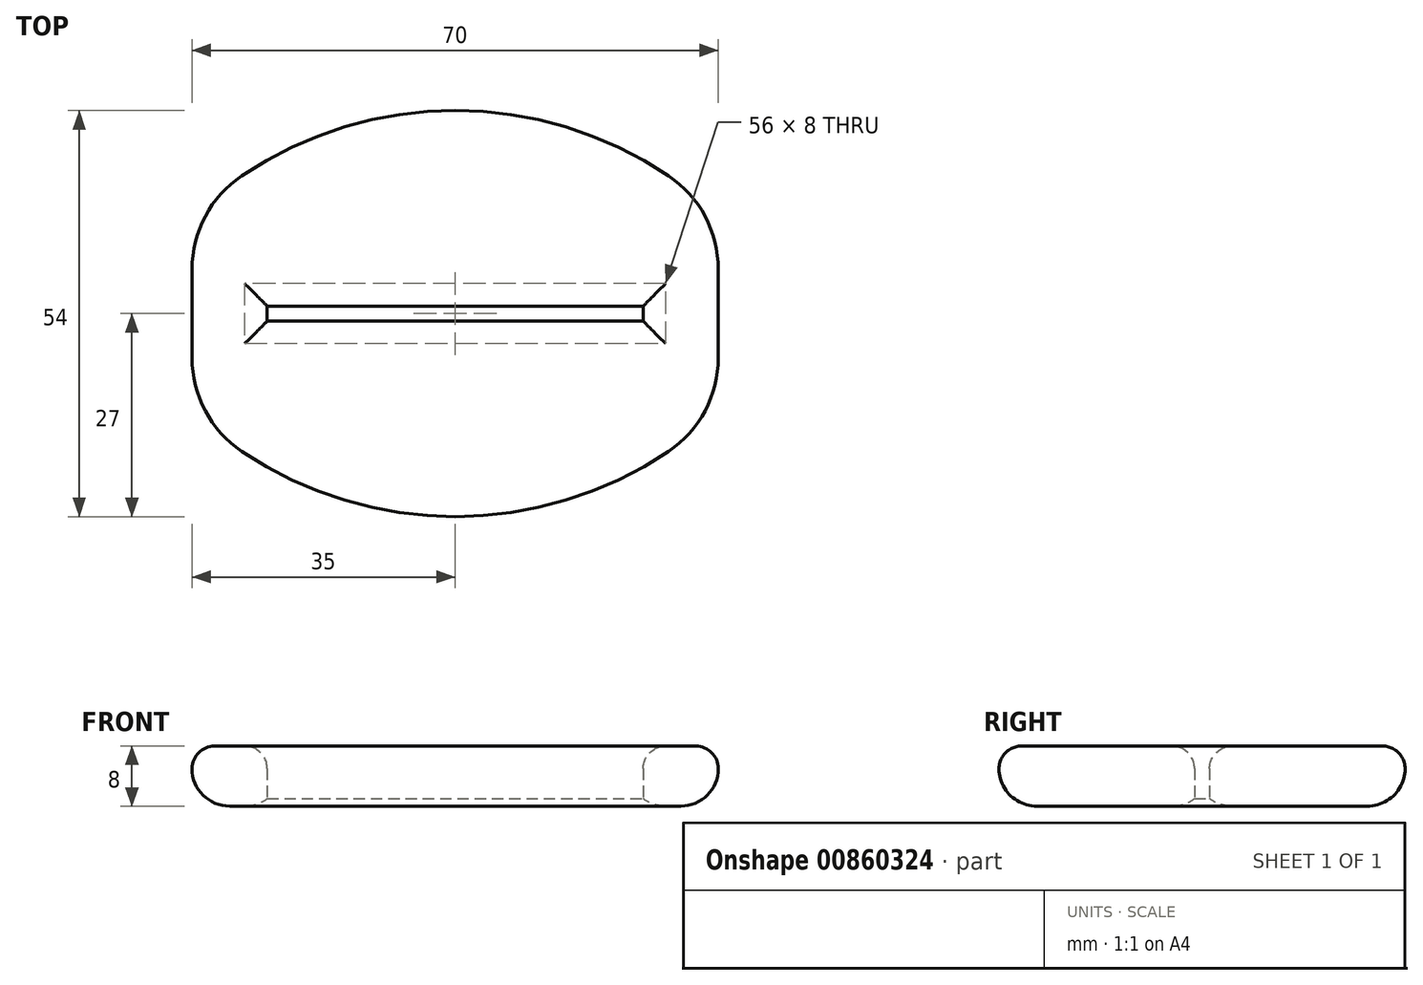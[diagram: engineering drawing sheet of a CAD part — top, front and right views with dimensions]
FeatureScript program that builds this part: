
annotation { "Feature Type Name" : "Feature", "Feature Type Description" : "" }
export const myFeature = defineFeature(function(context is Context, id is Id, definition is map)
    precondition{}
    {
        {
            var Q0;
            Q0=qCreatedBy(makeId("Top.planeOp"),FACE);
            var sketch = newSketch(context, id + "F0", { "sketchPlane" : qUnion([Q0])});
            skLineSegment(sketch, "E0.bottom", {"start": v(-25, 1) * mm, "end": v(25, 1) * mm});
            skLineSegment(sketch, "E0.top", {"start": v(-25, -1) * mm, "end": v(25, -1) * mm});
            skLineSegment(sketch, "E0.left", {"start": v(-25, 1) * mm, "end": v(-25, -1) * mm});
            skLineSegment(sketch, "E0.right", {"start": v(25, 1) * mm, "end": v(25, -1) * mm});
            skPoint(sketch, "E0.middle", {"position": v(0, 0) * mm});
            skLineSegment(sketch, "E1.bottom", {"start": v(-35, 13) * mm, "end": v(35, 13) * mm});
            skLineSegment(sketch, "E1.top", {"start": v(-35, -13) * mm, "end": v(35, -13) * mm});
            skLineSegment(sketch, "E1.left", {"start": v(-35, 13) * mm, "end": v(-35, -13) * mm});
            skLineSegment(sketch, "E1.right", {"start": v(35, 13) * mm, "end": v(35, -13) * mm});
            skArc(sketch, "E2", {"start": v(35, 13) * mm, "mid": v(0, 27) * mm, "end": v(-35, 13) * mm});
            skArc(sketch, "E3", {"start": v(-35, -13) * mm, "mid": v(0, -27) * mm, "end": v(35, -13) * mm});
            skSolve(sketch);
        }
        {
            var Q0;
            Q0=makeQuery(id+"F0.imprint","IMPRINT",FACE,{"disambiguationData":[TD([[makeQuery(id+"F0.imprint","IMPRINT",EDGE,{"derivedFrom":sQuery(id+"F0.wireOp",EDGE,"E1.bottom")}),1.0]])]});
            var Q1;
            Q1=makeQuery(id+"F0.imprint","IMPRINT",FACE,{"disambiguationData":[TD([[makeQuery(id+"F0.imprint","IMPRINT",EDGE,{"derivedFrom":sQuery(id+"F0.wireOp",EDGE,"E0.bottom")}),1.0]])]});
            var Q2;
            Q2=makeQuery(id+"F0.imprint","IMPRINT",FACE,{"disambiguationData":[TD([[makeQuery(id+"F0.imprint","IMPRINT",EDGE,{"derivedFrom":sQuery(id+"F0.wireOp",EDGE,"E1.top")}),-1.0]])]});
            extrude(context, id + "F1", {"entities" : qUnion([Q0, Q1, Q2]), "depth" : 8 * mm, "offsetDistance" : 25 * mm});
        }
        {
            var Q0;
            Q0=makeQuery(id+"F1.opExtrude","CAP_FACE",FACE,{"disambiguationData":[OSD([sQuery(id+"F0.wireOp",EDGE,"E0.bottom"),sQuery(id+"F0.wireOp",EDGE,"E0.top"),sQuery(id+"F0.wireOp",EDGE,"E0.left"),sQuery(id+"F0.wireOp",EDGE,"E0.right"),sQuery(id+"F0.wireOp",EDGE,"E1.bottom"),sQuery(id+"F0.wireOp",EDGE,"E1.top"),sQuery(id+"F0.wireOp",EDGE,"E1.left"),sQuery(id+"F0.wireOp",EDGE,"E1.right")])],"isStart":false});
            fillet(context, id + "F2", {"entities" : qUnion([Q0]), "radius" : 3 * mm, "tangentPropagation" : true, "allowEdgeOverflow" : false});
        }
        {
            var Q0;
            Q0=makeQuery(id+"F2.opFillet","BLEND_EDGE",EDGE,{"blendedFrom":[makeQuery(id+"F1.opExtrude","CAP_EDGE",EDGE,{"disambiguationData":[OSD([sQuery(id+"F0.wireOp",EDGE,"E1.left")])],"isStart":false}),makeQuery(id+"F1.opExtrude","CAP_EDGE",EDGE,{"disambiguationData":[OSD([sQuery(id+"F0.wireOp",EDGE,"E3")])],"isStart":false})],"blendedInto":[]});
            var Q1;
            Q1=makeQuery(id+"F1.opExtrude","SWEPT_EDGE",EDGE,{"disambiguationData":[OSD([sQuery(id+"F0.wireOp",EDGE,"E1.top"),sQuery(id+"F0.wireOp",EDGE,"E1.left"),sQuery(id+"F0.wireOp",EDGE,"E3")])]});
            var Q2;
            Q2=makeQuery(id+"F1.opExtrude","SWEPT_EDGE",EDGE,{"disambiguationData":[OSD([sQuery(id+"F0.wireOp",EDGE,"E1.bottom"),sQuery(id+"F0.wireOp",EDGE,"E1.left"),sQuery(id+"F0.wireOp",EDGE,"E2")])]});
            var Q3;
            Q3=makeQuery(id+"F2.opFillet","BLEND_EDGE",EDGE,{"blendedFrom":[makeQuery(id+"F1.opExtrude","CAP_EDGE",EDGE,{"disambiguationData":[OSD([sQuery(id+"F0.wireOp",EDGE,"E1.left")])],"isStart":false}),makeQuery(id+"F1.opExtrude","CAP_EDGE",EDGE,{"disambiguationData":[OSD([sQuery(id+"F0.wireOp",EDGE,"E2")])],"isStart":false})],"blendedInto":[]});
            var Q4;
            Q4=makeQuery(id+"F1.opExtrude","SWEPT_EDGE",EDGE,{"disambiguationData":[OSD([sQuery(id+"F0.wireOp",EDGE,"E1.top"),sQuery(id+"F0.wireOp",EDGE,"E1.right"),sQuery(id+"F0.wireOp",EDGE,"E3")])]});
            var Q5;
            Q5=makeQuery(id+"F1.opExtrude","SWEPT_EDGE",EDGE,{"disambiguationData":[OSD([sQuery(id+"F0.wireOp",EDGE,"E1.bottom"),sQuery(id+"F0.wireOp",EDGE,"E1.right"),sQuery(id+"F0.wireOp",EDGE,"E2")])]});
            fillet(context, id + "F3", {"entities" : qUnion([Q0, Q1, Q2, Q3, Q4, Q5]), "radius" : 15 * mm, "tangentPropagation" : true, "allowEdgeOverflow" : false});
        }
        {
            var Q0;
            Q0=makeQuery(id+"F1.opExtrude","CAP_EDGE",EDGE,{"disambiguationData":[OSD([sQuery(id+"F0.wireOp",EDGE,"E0.bottom")])],"isStart":true});
            var Q1;
            Q1=makeQuery(id+"F1.opExtrude","CAP_EDGE",EDGE,{"disambiguationData":[OSD([sQuery(id+"F0.wireOp",EDGE,"E0.right")])],"isStart":true});
            var Q2;
            Q2=makeQuery(id+"F1.opExtrude","CAP_EDGE",EDGE,{"disambiguationData":[OSD([sQuery(id+"F0.wireOp",EDGE,"E0.top")])],"isStart":true});
            var Q3;
            Q3=makeQuery(id+"F1.opExtrude","CAP_EDGE",EDGE,{"disambiguationData":[OSD([sQuery(id+"F0.wireOp",EDGE,"E0.left")])],"isStart":true});
            chamfer(context, id + "F4", {"entities" : qUnion([Q0, Q1, Q2, Q3]), "width" : 1 * mm, "tangentPropagation" : true});
        }
        {
            var Q0;
            Q0=makeQuery(id+"F1.opExtrude","CAP_FACE",FACE,{"disambiguationData":[OSD([sQuery(id+"F0.wireOp",EDGE,"E0.bottom"),sQuery(id+"F0.wireOp",EDGE,"E0.top"),sQuery(id+"F0.wireOp",EDGE,"E0.left"),sQuery(id+"F0.wireOp",EDGE,"E0.right"),sQuery(id+"F0.wireOp",EDGE,"E1.left"),sQuery(id+"F0.wireOp",EDGE,"E1.right"),sQuery(id+"F0.wireOp",EDGE,"E2"),sQuery(id+"F0.wireOp",EDGE,"E3")])],"isStart":true});
            fillet(context, id + "F5", {"entities" : qUnion([Q0]), "radius" : 5 * mm, "tangentPropagation" : true, "allowEdgeOverflow" : false});
        }
    });
